# Revit family: HansWeitzel_52529
name_source: partatom
category: Allgemeines Modell
revit_build: Autodesk Revit 2017 (Build: 20160225_1515(x64)
units: mm (PartAtom-declared; Revit-internal decimal feet)

## family parameters
Basisbauteil = Wand
Beim Laden mit Abzugskörper schneiden = Nein
Bemaßung runder Anschluss = Durchmesser verwenden
Gemeinsam genutzt = Nein
Immer vertikal = Ja
Kann Basisbauteil für Bewehrung sein = Nein
Raumberechnungspunkt = Nein
Teiletyp = Normal

## types (1)
- HansWeitzel_52529
    BIM = https://media.live.bim.site
    BIMSITE_PRODUCT_ID = 44566f69d7faec249ec2fe52af7c7b477cf8e39a
    Beschreibung = HZ-Blindleiste BLF Alu, 2m mit Dekorfolie passend zu SLF AL
    Brandklasse B2 = Ja
    Breite [mm] = 2000
    Dekor = Alu
    Farbton = metallfarben
    GTIN = 4022023113617
    Gewicht unverpackt (netto) [kg] = 0.7
    HAN = 52529
    HeinzeBIM = https://www.heinze.de
    Hersteller = Hans Weitzel GmbH & Co. KG
    Höhe [mm] = 87
    Ist System = Nein
    Ist Zubehör = Nein
    Menge pro Verpackungseinheit = 10
    Profilart = Sockelprofil
    Selbstverlöschend = Ja
    Tiefe (mm) = 16
    Typname = HZ-Blindleiste BLF Alu, 2m
    Wandmontage möglich = Ja
    Werkstoff = PVC
    max. Betriebstemperatur (°C) = 90

## geometry (parser evidence)
native form markers: Sweep x5
no freeform markers — native parametric forms only
